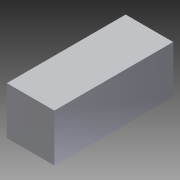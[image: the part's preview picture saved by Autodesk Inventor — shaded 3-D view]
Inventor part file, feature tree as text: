
AUTODESK INVENTOR PART (.ipt)
format: ipt  version: 2014 SP1 (Build 180222100, 222)  size: 71,680 bytes
history: native  units: in
note: dims shown in document units (in); Inventor stores cm internally (conversion verified against a paired STEP export)
features: extrude x1, sketch x1
ambient origin geometry x8: Origin, YZ Plane, XZ Plane, XY Plane, X Axis, Y Axis, Z Axis, Center Point
bodies: Solid1 (feature_tree)
feature tree (2):
  extrude  "Extrusion1"  Depth=236.2205in
  sketch  "Sketch1"  dims[d0=94.4882in d1=236.2205in d2=94.4882in d3=0.0in]
